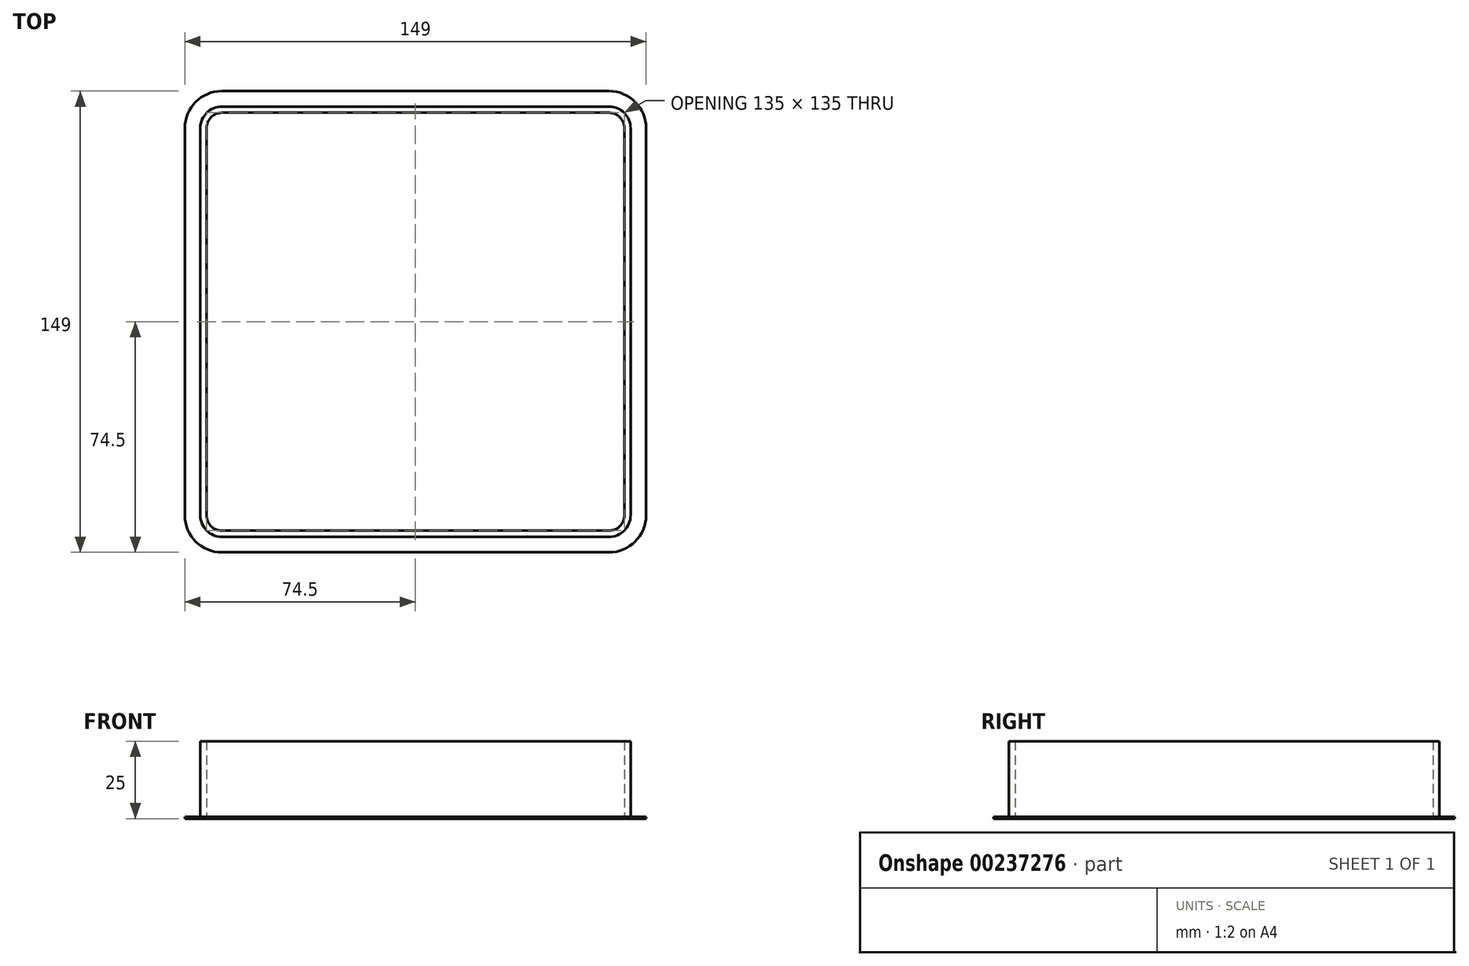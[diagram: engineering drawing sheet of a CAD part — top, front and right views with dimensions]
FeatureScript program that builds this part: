
annotation { "Feature Type Name" : "Feature", "Feature Type Description" : "" }
export const myFeature = defineFeature(function(context is Context, id is Id, definition is map)
    precondition{}
    {
        {
            var Q0;
            Q0=qCreatedBy(makeId("Top.planeOp"),FACE);
            var sketch = newSketch(context, id + "F0", { "sketchPlane" : qUnion([Q0])});
            skLineSegment(sketch, "E0.bottom", {"start": v(62.5, 67.5) * mm, "end": v(-62.5, 67.5) * mm});
            skLineSegment(sketch, "E0.top", {"start": v(62.5, -67.5) * mm, "end": v(-62.5, -67.5) * mm});
            skLineSegment(sketch, "E0.left", {"start": v(67.5, 62.5) * mm, "end": v(67.5, -62.5) * mm});
            skLineSegment(sketch, "E0.right", {"start": v(-67.5, 62.5) * mm, "end": v(-67.5, -62.5) * mm});
            skPoint(sketch, "E0.middle", {"position": v(0, 0) * mm});
            skPoint(sketch, "E1.visualSharp", {"position": v(-67.5, 67.5) * mm});
            skArc(sketch, "E1.filletArc", {"start": v(-62.5, 67.5) * mm, "mid": v(-66.04, 66.04) * mm, "end": v(-67.5, 62.5) * mm});
            skPoint(sketch, "E2.visualSharp", {"position": v(67.5, 67.5) * mm});
            skArc(sketch, "E2.filletArc", {"start": v(67.5, 62.5) * mm, "mid": v(66.04, 66.04) * mm, "end": v(62.5, 67.5) * mm});
            skPoint(sketch, "E3.visualSharp", {"position": v(-67.5, -67.5) * mm});
            skArc(sketch, "E3.filletArc", {"start": v(-67.5, -62.5) * mm, "mid": v(-66.04, -66.04) * mm, "end": v(-62.5, -67.5) * mm});
            skPoint(sketch, "E4.visualSharp", {"position": v(67.5, -67.5) * mm});
            skArc(sketch, "E4.filletArc", {"start": v(62.5, -67.5) * mm, "mid": v(66.04, -66.04) * mm, "end": v(67.5, -62.5) * mm});
            skArc(sketch, "E5.0", {"start": v(69.5, 62.5) * mm, "mid": v(67.45, 67.45) * mm, "end": v(62.5, 69.5) * mm});
            skLineSegment(sketch, "E5.1", {"start": v(69.5, 62.5) * mm, "end": v(69.5, -62.5) * mm});
            skLineSegment(sketch, "E5.2", {"start": v(62.5, 69.5) * mm, "end": v(-62.5, 69.5) * mm});
            skArc(sketch, "E5.3", {"start": v(62.5, -69.5) * mm, "mid": v(67.45, -67.45) * mm, "end": v(69.5, -62.5) * mm});
            skArc(sketch, "E5.4", {"start": v(-62.5, 69.5) * mm, "mid": v(-67.45, 67.45) * mm, "end": v(-69.5, 62.5) * mm});
            skLineSegment(sketch, "E5.5", {"start": v(-69.5, 62.5) * mm, "end": v(-69.5, -62.5) * mm});
            skArc(sketch, "E5.6", {"start": v(-69.5, -62.5) * mm, "mid": v(-67.45, -67.45) * mm, "end": v(-62.5, -69.5) * mm});
            skLineSegment(sketch, "E5.7", {"start": v(62.5, -69.5) * mm, "end": v(-62.5, -69.5) * mm});
            skArc(sketch, "E6.0", {"start": v(74.5, 62.5) * mm, "mid": v(70.99, 70.99) * mm, "end": v(62.5, 74.5) * mm});
            skLineSegment(sketch, "E6.1", {"start": v(74.5, 62.5) * mm, "end": v(74.5, -62.5) * mm});
            skLineSegment(sketch, "E6.2", {"start": v(62.5, 74.5) * mm, "end": v(-62.5, 74.5) * mm});
            skArc(sketch, "E6.3", {"start": v(62.5, -74.5) * mm, "mid": v(70.99, -70.99) * mm, "end": v(74.5, -62.5) * mm});
            skArc(sketch, "E6.4", {"start": v(-62.5, 74.5) * mm, "mid": v(-70.99, 70.99) * mm, "end": v(-74.5, 62.5) * mm});
            skLineSegment(sketch, "E6.5", {"start": v(-74.5, 62.5) * mm, "end": v(-74.5, -62.5) * mm});
            skArc(sketch, "E6.6", {"start": v(-74.5, -62.5) * mm, "mid": v(-70.99, -70.99) * mm, "end": v(-62.5, -74.5) * mm});
            skLineSegment(sketch, "E6.7", {"start": v(62.5, -74.5) * mm, "end": v(-62.5, -74.5) * mm});
            skSolve(sketch);
        }
        {
            var Q0;
            Q0=makeQuery(id+"F0.imprint","IMPRINT",FACE,{"disambiguationData":[TD([[makeQuery(id+"F0.imprint","IMPRINT",EDGE,{"derivedFrom":sQuery(id+"F0.wireOp",EDGE,"E0.bottom")}),-1.0]])]});
            extrude(context, id + "F1", {"entities" : qUnion([Q0]), "depth" : 25 * mm});
        }
        {
            var Q0;
            Q0=makeQuery(id+"F0.imprint","IMPRINT",FACE,{"disambiguationData":[TD([[makeQuery(id+"F0.imprint","IMPRINT",EDGE,{"derivedFrom":sQuery(id+"F0.wireOp",EDGE,"E5.0")}),-1.0]])]});
            extrude(context, id + "F2", {"entities" : qUnion([Q0]), "operationType" : NewBodyOperationType.ADD, "depth" : 0.6 * mm});
        }
    });
